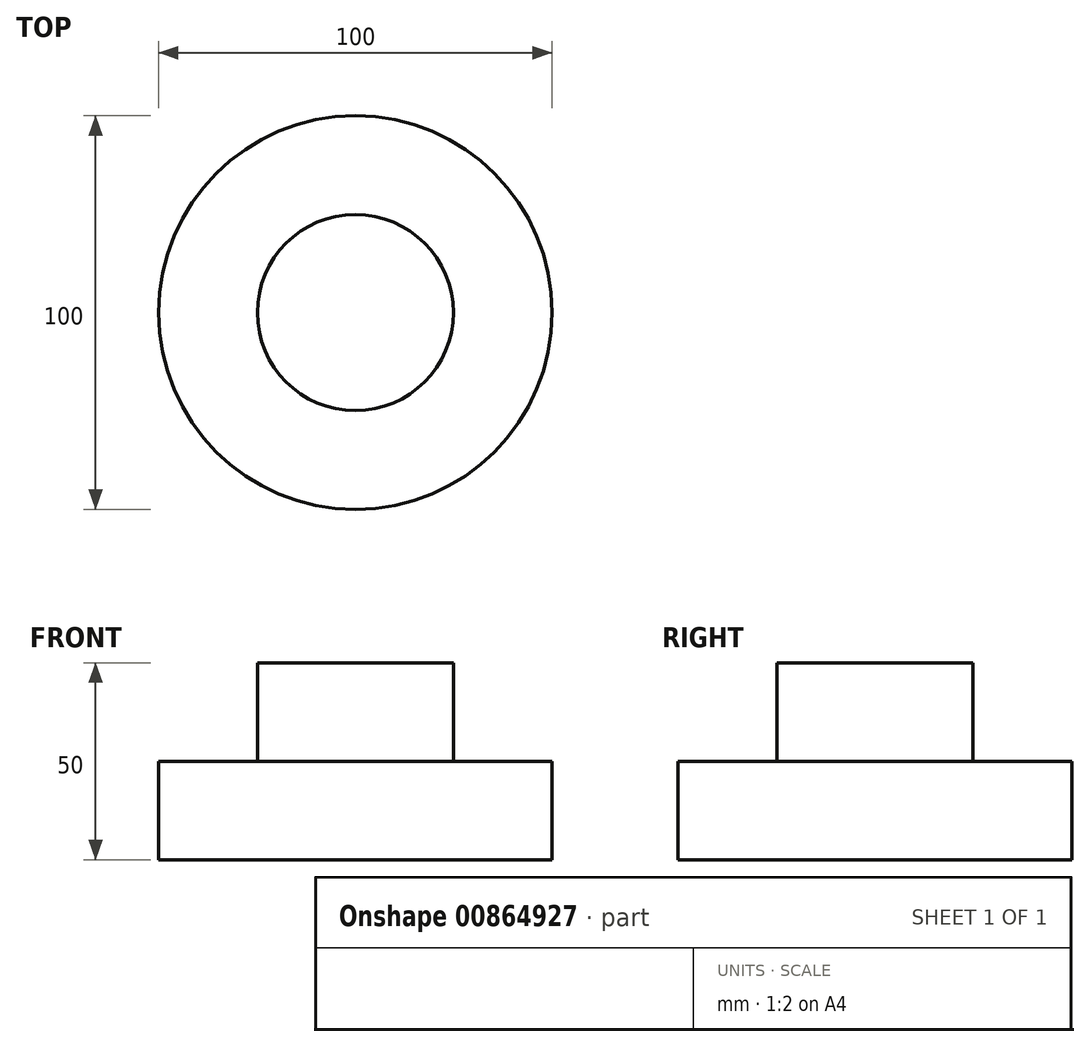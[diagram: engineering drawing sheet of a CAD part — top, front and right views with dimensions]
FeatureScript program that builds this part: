
annotation { "Feature Type Name" : "Feature", "Feature Type Description" : "" }
export const myFeature = defineFeature(function(context is Context, id is Id, definition is map)
    precondition{}
    {
        {
            var Q0;
            Q0=qCreatedBy(makeId("Top.planeOp"),FACE);
            var sketch = newSketch(context, id + "F0", { "sketchPlane" : qUnion([Q0])});
            skCircle(sketch, "E0", {"center": v(0, 0) * mm, "radius": 50 * mm});
            skSolve(sketch);
        }
        {
            var Q0;
            Q0=makeQuery(id+"F0.imprint","IMPRINT",FACE,{"disambiguationData":[TD([[makeQuery(id+"F0.imprint","IMPRINT",EDGE,{"derivedFrom":sQuery(id+"F0.wireOp",EDGE,"E0")}),1.0]])]});
            var Q1;
            Q1=sQuery(id+"F0.wireOp",EDGE,"E0");
            extrude(context, id + "F1", {"entities" : qUnion([Q0]), "surfaceEntities" : qUnion([Q1]), "depth" : 25 * mm, "offsetDistance" : 25 * mm});
        }
        {
            var Q0;
            Q0=makeQuery(id+"F1.opExtrude","CAP_FACE",FACE,{"disambiguationData":[OSD([sQuery(id+"F0.wireOp",EDGE,"E0")])],"isStart":false});
            var sketch = newSketch(context, id + "F2", { "sketchPlane" : qUnion([Q0])});
            skCircle(sketch, "E1", {"center": v(0, 0) * mm, "radius": 24.91 * mm});
            skSolve(sketch);
        }
        {
            var Q0;
            Q0=makeQuery(id+"F2.imprint","IMPRINT",FACE,{"disambiguationData":[TD([[makeQuery(id+"F2.imprint","IMPRINT",EDGE,{"derivedFrom":sQuery(id+"F2.wireOp",EDGE,"E1")}),1.0]])]});
            extrude(context, id + "F3", {"entities" : qUnion([Q0]), "depth" : 25 * mm, "offsetDistance" : 25 * mm});
        }
    });
